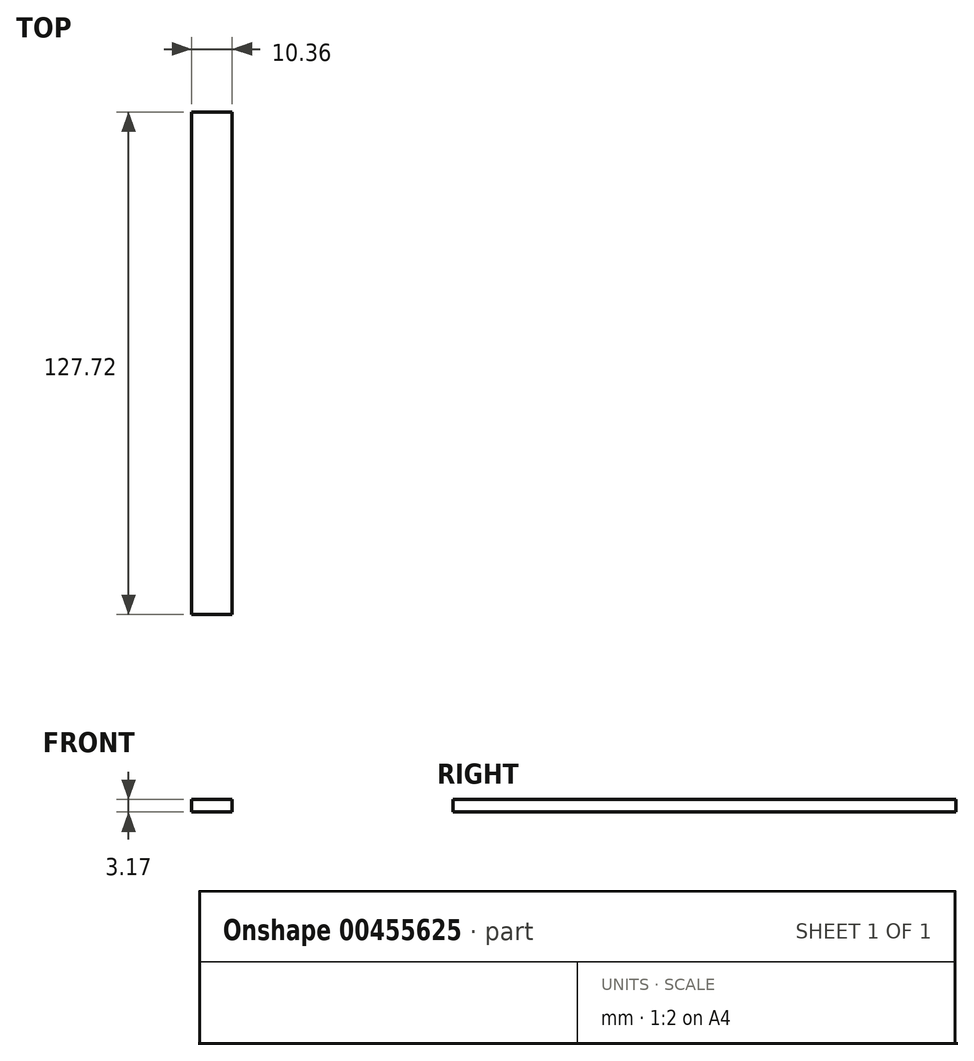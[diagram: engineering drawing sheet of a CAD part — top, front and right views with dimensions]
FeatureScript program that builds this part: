
annotation { "Feature Type Name" : "Feature", "Feature Type Description" : "" }
export const myFeature = defineFeature(function(context is Context, id is Id, definition is map)
    precondition{}
    {
        {
            var Q0;
            Q0=qCreatedBy(makeId("Top.planeOp"),FACE);
            var sketch = newSketch(context, id + "F0", { "sketchPlane" : qUnion([Q0])});
            skLineSegment(sketch, "E0.bottom", {"start": v(5.18, 63.86) * mm, "end": v(-5.18, 63.86) * mm});
            skLineSegment(sketch, "E0.top", {"start": v(5.18, -63.86) * mm, "end": v(-5.18, -63.86) * mm});
            skLineSegment(sketch, "E0.left", {"start": v(5.18, 63.86) * mm, "end": v(5.18, -63.86) * mm});
            skLineSegment(sketch, "E0.right", {"start": v(-5.18, 63.86) * mm, "end": v(-5.18, -63.86) * mm});
            skPoint(sketch, "E0.middle", {"position": v(0, 0) * mm});
            skSolve(sketch);
        }
        {
            var Q0;
            Q0=makeQuery(id+"F0.imprint","IMPRINT",FACE,{"disambiguationData":[TD([[makeQuery(id+"F0.imprint","IMPRINT",EDGE,{"derivedFrom":sQuery(id+"F0.wireOp",EDGE,"E0.bottom")}),1.0]])]});
            extrude(context, id + "F1", {"entities" : qUnion([Q0]), "depth" : 3.17 * mm});
        }
    });
